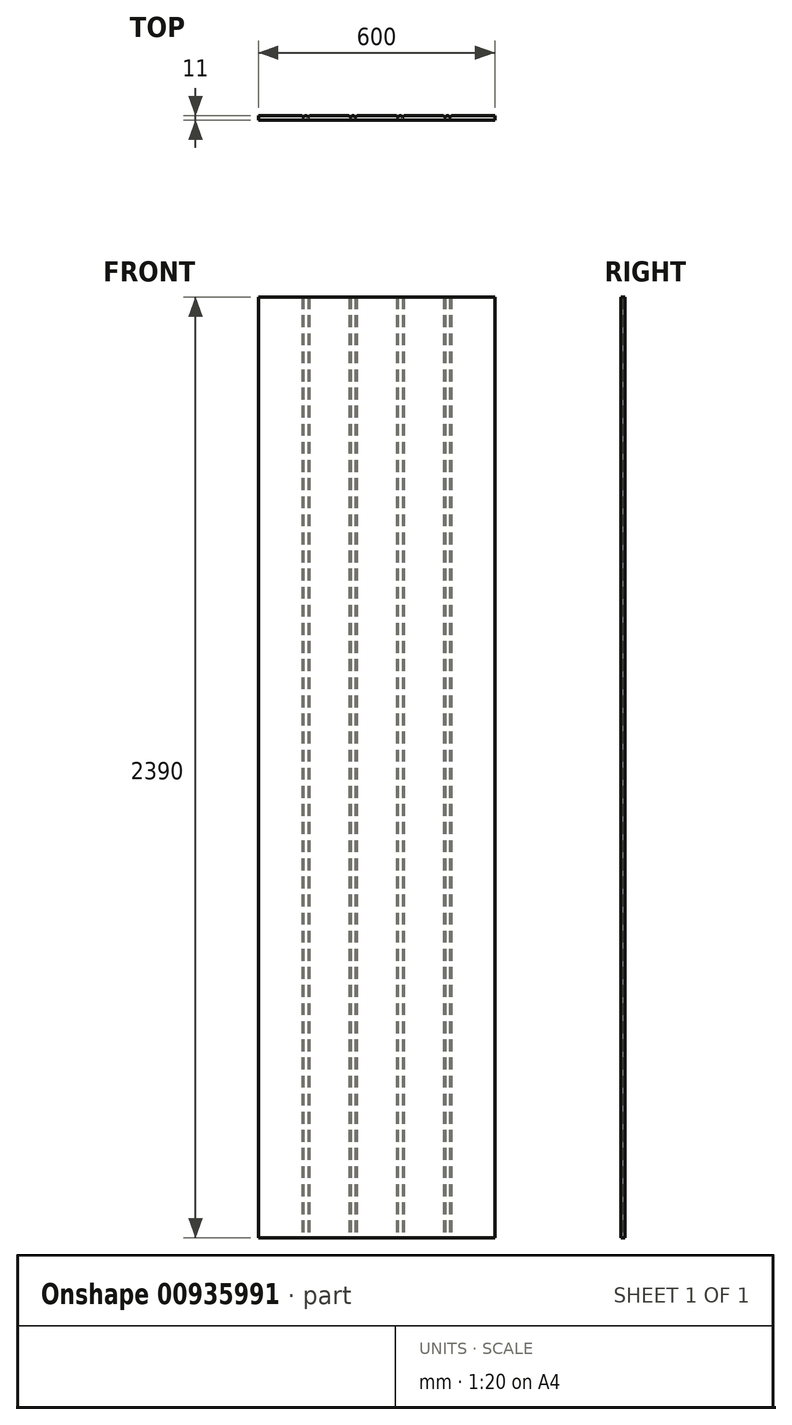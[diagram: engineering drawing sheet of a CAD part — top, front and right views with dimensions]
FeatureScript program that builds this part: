
annotation { "Feature Type Name" : "Feature", "Feature Type Description" : "" }
export const myFeature = defineFeature(function(context is Context, id is Id, definition is map)
    precondition{}
    {
        {
            var Q0;
            Q0=qCreatedBy(makeId("Top.planeOp"),FACE);
            var sketch = newSketch(context, id + "F0", { "sketchPlane" : qUnion([Q0])});
            skLineSegment(sketch, "E0.bottom", {"start": v(290.5, -5.5) * mm, "end": v(-309.5, -5.5) * mm});
            skLineSegment(sketch, "E0.right", {"start": v(-309.5, -5.5) * mm, "end": v(-309.5, 5.5) * mm});
            skPoint(sketch, "E0.middle", {"position": v(0, 0) * mm});
            skLineSegment(sketch, "E1", {"start": v(-189.5, 5.5) * mm, "end": v(-189.5, 0) * mm, "construction": true});
            skLineSegment(sketch, "E2", {"start": v(-69.5, 5.5) * mm, "end": v(-69.5, 0) * mm});
            skLineSegment(sketch, "E3", {"start": v(50.5, 5.5) * mm, "end": v(50.5, 0) * mm});
            skLineSegment(sketch, "E4", {"start": v(290.5, 5.5) * mm, "end": v(290.5, -5.5) * mm});
            skArc(sketch, "E5", {"start": v(-184, 0) * mm, "mid": v(-189.5, 5.5) * mm, "end": v(-195, 0) * mm});
            skArc(sketch, "E6", {"start": v(-64, 0) * mm, "mid": v(-69.5, 5.5) * mm, "end": v(-75, 0) * mm});
            skArc(sketch, "E7", {"start": v(56, 0) * mm, "mid": v(50.5, 5.5) * mm, "end": v(45, 0) * mm});
            skArc(sketch, "E8", {"start": v(176, 0) * mm, "mid": v(170.5, 5.5) * mm, "end": v(165, 0) * mm});
            skArc(sketch, "E9", {"start": v(290.5, 5.5) * mm, "mid": v(285, 0) * mm, "end": v(290.5, -5.5) * mm});
            skLineSegment(sketch, "E10", {"start": v(160.5, 5.5) * mm, "end": v(160.5, -5.5) * mm, "construction": true});
            skLineSegment(sketch, "E11", {"start": v(180.5, 5.5) * mm, "end": v(180.5, -5.5) * mm, "construction": true});
            skLineSegment(sketch, "E12", {"start": v(165, 0) * mm, "end": v(160.5, 5.5) * mm});
            skLineSegment(sketch, "E13", {"start": v(176, 0) * mm, "end": v(180.5, 5.5) * mm});
            skPoint(sketch, "E13.startSnap0", {"position": v(180.5, 0) * mm});
            skPoint(sketch, "E14.start.orphan", {"position": v(170.5, 5.5) * mm});
            skPoint(sketch, "E15.orphan", {"position": v(170.5, -5.5) * mm});
            skLineSegment(sketch, "E16", {"start": v(278.7, 5.5) * mm, "end": v(278.7, -5.5) * mm, "construction": true});
            skLineSegment(sketch, "E17", {"start": v(56, 0) * mm, "end": v(60.5, 5.5) * mm});
            skLineSegment(sketch, "E18", {"start": v(40.5, 5.5) * mm, "end": v(45, 0) * mm});
            skLineSegment(sketch, "E19", {"start": v(-64, 0) * mm, "end": v(-59.5, 5.5) * mm});
            skLineSegment(sketch, "E20", {"start": v(-79.5, 5.5) * mm, "end": v(-75, 0) * mm});
            skLineSegment(sketch, "E21", {"start": v(-199.5, 5.5) * mm, "end": v(-195, 0) * mm});
            skLineSegment(sketch, "E22", {"start": v(-179.5, 5.5) * mm, "end": v(-184, 0) * mm});
            skLineSegment(sketch, "E23.trimOffspring", {"start": v(160.5, 5.5) * mm, "end": v(60.5, 5.5) * mm});
            skLineSegment(sketch, "E24.trimOffspring", {"start": v(40.5, 5.5) * mm, "end": v(-59.5, 5.5) * mm});
            skLineSegment(sketch, "E25.trimOffspring", {"start": v(-79.5, 5.5) * mm, "end": v(-179.5, 5.5) * mm});
            skLineSegment(sketch, "E26.trimOffspring", {"start": v(-199.5, 5.5) * mm, "end": v(-309.5, 5.5) * mm});
            skLineSegment(sketch, "E27.trimOffspring", {"start": v(290.5, 5.5) * mm, "end": v(180.5, 5.5) * mm});
            skPoint(sketch, "E28.orphan", {"position": v(-189.5, -5.5) * mm});
            skPoint(sketch, "E29.orphan", {"position": v(-69.5, -5.5) * mm});
            skPoint(sketch, "E30.orphan", {"position": v(50.5, -5.5) * mm});
            skPoint(sketch, "E31.start.orphan", {"position": v(296, 0) * mm});
            skPoint(sketch, "E0.left.end.orphan", {"position": v(309.5, 5.5) * mm});
            skPoint(sketch, "E32.orphan", {"position": v(309.5, -5.5) * mm});
            skSolve(sketch);
        }
        {
            var Q0;
            {var subQ12=sQuery(id+"F0.wireOp",EDGE,"E0.right");Q0=makeQuery(id+"F0.imprint","IMPRINT",FACE,{"disambiguationData":[TD([[makeQuery(id+"F0.imprint","IMPRINT",EDGE,{"derivedFrom":subQ12}),-1.0]])]});}
            var Q1;
            {var subQ0=sQuery(id+"F0.wireOp",EDGE,"E4");Q1=makeQuery(id+"F0.imprint","IMPRINT",FACE,{"disambiguationData":[TD([[makeQuery(id+"F0.imprint","IMPRINT",EDGE,{"derivedFrom":subQ0}),1.0]])]});}
            var Q2;
            {var subQ3=sQuery(id+"F0.wireOp",EDGE,"I1rh5Qsn-RcJP-wCtw-Ny6q-KbmPlX2Gdoi8");Q2=makeQuery(id+"F0.imprint","IMPRINT",FACE,{"disambiguationData":[TD([[makeQuery(id+"F0.imprint","IMPRINT",EDGE,{"derivedFrom":subQ3}),-1.0]])]});}
            var Q3;
            Q3=makeQuery(id+"F0.imprint","IMPRINT",FACE,{"disambiguationData":[TD([[makeQuery(id+"F0.imprint","IMPRINT",EDGE,{"derivedFrom":sQuery(id+"F0.wireOp",EDGE,"E0.top")}),1.0]])]});
            var Q4;
            {var subQ0=sQuery(id+"F0.wireOp",EDGE,"E4");Q4=makeQuery(id+"F0.imprint","IMPRINT",FACE,{"disambiguationData":[TD([[makeQuery(id+"F0.imprint","IMPRINT",EDGE,{"derivedFrom":subQ0}),-1.0]])]});}
            extrude(context, id + "F1", {"entities" : qUnion([Q0, Q1, Q2, Q3, Q4]), "depth" : 2390 * mm, "offsetDistance" : 25 * mm});
        }
    });
